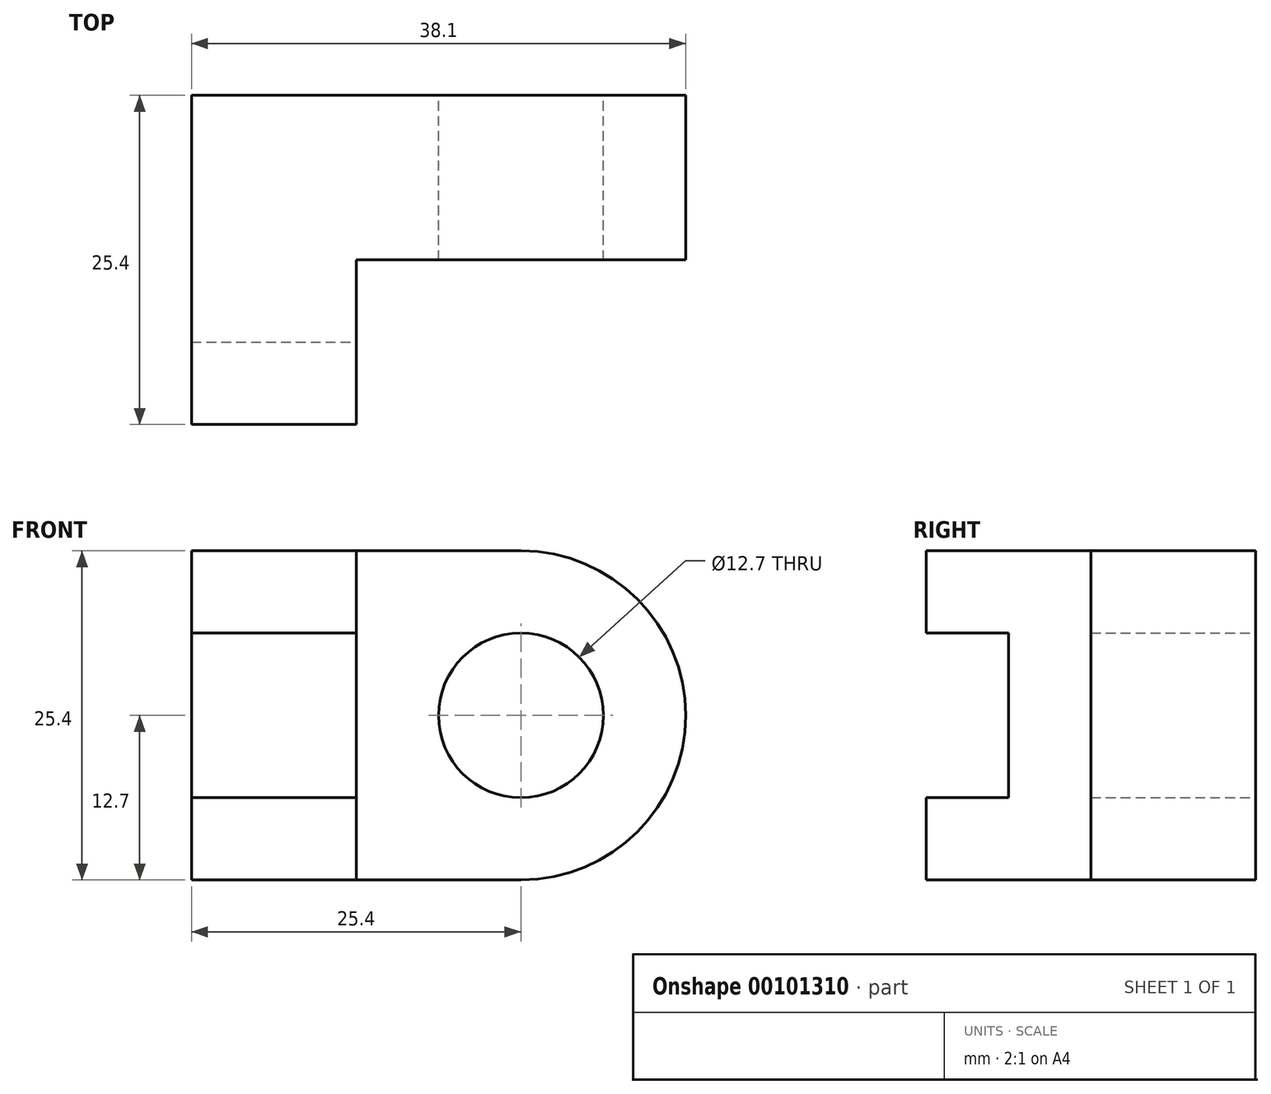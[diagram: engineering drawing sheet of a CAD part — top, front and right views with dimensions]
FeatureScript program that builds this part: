
annotation { "Feature Type Name" : "Feature", "Feature Type Description" : "" }
export const myFeature = defineFeature(function(context is Context, id is Id, definition is map)
    precondition{}
    {
        {
            var Q0;
            Q0=qCreatedBy(makeId("Top.planeOp"),FACE);
            var sketch = newSketch(context, id + "F0", { "sketchPlane" : qUnion([Q0])});
            skLineSegment(sketch, "E0", {"start": v(-25.4, 0) * mm, "end": v(-25.4, 25.4) * mm});
            skLineSegment(sketch, "E1", {"start": v(-25.4, 25.4) * mm, "end": v(-38.1, 25.4) * mm});
            skLineSegment(sketch, "E2", {"start": v(-38.1, 25.4) * mm, "end": v(-38.1, 0) * mm});
            skLineSegment(sketch, "E3", {"start": v(-38.1, 0) * mm, "end": v(-25.4, 0) * mm});
            skSolve(sketch);
        }
        {
            var Q0;
            Q0 = qSketchRegion(id + "F0", true);
            extrude(context, id + "F1", {"entities" : qUnion([Q0]), "depth" : 25.4 * mm});
        }
        {
            var Q0;
            Q0=qCreatedBy(makeId("Right.planeOp"),FACE);
            var sketch = newSketch(context, id + "F2", { "sketchPlane" : qUnion([Q0])});
            skLineSegment(sketch, "E4", {"start": v(0, 19.05) * mm, "end": v(6.35, 19.05) * mm});
            skLineSegment(sketch, "E5", {"start": v(6.35, 19.05) * mm, "end": v(6.35, 6.35) * mm});
            skLineSegment(sketch, "E6", {"start": v(6.35, 6.35) * mm, "end": v(0, 6.35) * mm});
            skLineSegment(sketch, "E7", {"start": v(0, 6.35) * mm, "end": v(0, 19.05) * mm});
            skSolve(sketch);
        }
        {
            var Q0;
            Q0 = qSketchRegion(id + "F2", true);
            extrude(context, id + "F3", {"entities" : qUnion([Q0]), "operationType" : NewBodyOperationType.REMOVE, "endBound" : BoundingType.THROUGH_ALL, "oppositeDirection" : true, "depth" : 25.4 * mm});
        }
        {
            var Q0;
            Q0=makeQuery(id+"F1.opExtrude","SWEPT_FACE",FACE,{"disambiguationData":[OSD([sQuery(id+"F0.wireOp",EDGE,"E1")])]});
            var sketch = newSketch(context, id + "F4", { "sketchPlane" : qUnion([Q0])});
            skLineSegment(sketch, "E8", {"start": v(12.7, 25.4) * mm, "end": v(38.1, 25.4) * mm});
            skLineSegment(sketch, "E9", {"start": v(38.1, 25.4) * mm, "end": v(38.1, 0) * mm});
            skLineSegment(sketch, "E10", {"start": v(38.1, 0) * mm, "end": v(12.7, 0) * mm});
            skArc(sketch, "E11", {"start": v(12.7, 25.4) * mm, "mid": v(0, 12.7) * mm, "end": v(12.7, 0) * mm});
            skCircle(sketch, "E12", {"center": v(12.7, 12.7) * mm, "radius": 6.35 * mm});
            skSolve(sketch);
        }
        {
            var Q0;
            Q0 = qSketchRegion(id + "F4", true);
            extrude(context, id + "F5", {"entities" : qUnion([Q0]), "operationType" : NewBodyOperationType.ADD, "oppositeDirection" : true, "depth" : 12.7 * mm});
        }
    });
